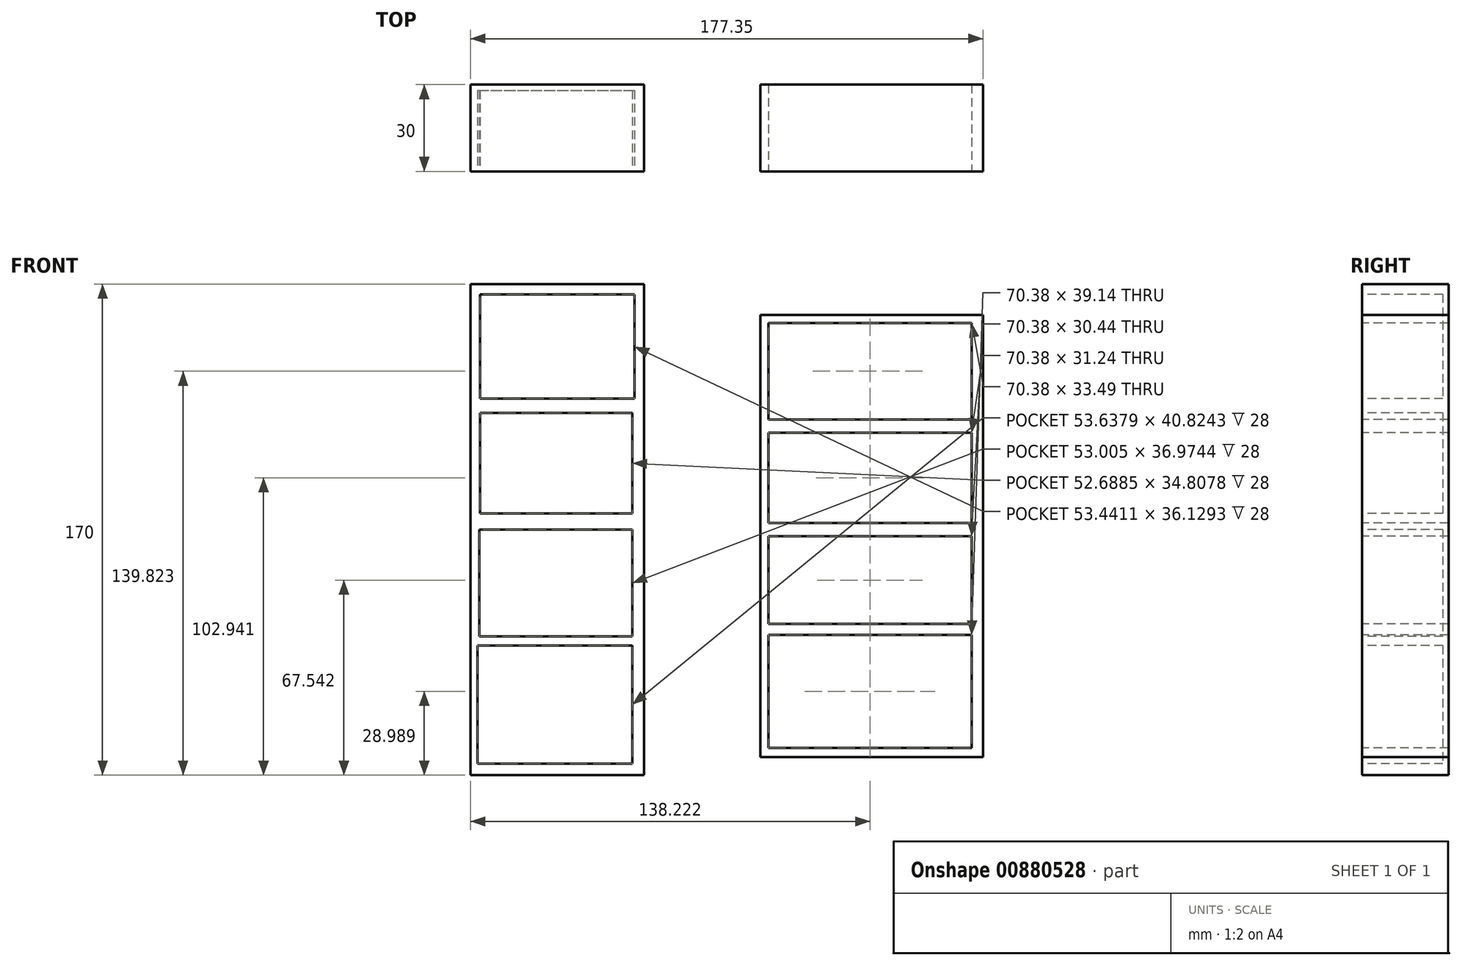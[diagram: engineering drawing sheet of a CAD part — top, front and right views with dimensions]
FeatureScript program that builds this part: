
annotation { "Feature Type Name" : "Feature", "Feature Type Description" : "" }
export const myFeature = defineFeature(function(context is Context, id is Id, definition is map)
    precondition{}
    {
        {
            var Q0;
            Q0=qCreatedBy(makeId("Front.planeOp"),FACE);
            var sketch = newSketch(context, id + "F0", { "sketchPlane" : qUnion([Q0])});
            skLineSegment(sketch, "E0.bottom", {"start": v(-219.84, 79.38) * mm, "end": v(-159.84, 79.38) * mm});
            skLineSegment(sketch, "E0.top", {"start": v(-219.84, -90.62) * mm, "end": v(-159.84, -90.62) * mm});
            skLineSegment(sketch, "E0.left", {"start": v(-219.84, 79.38) * mm, "end": v(-219.84, -90.62) * mm});
            skLineSegment(sketch, "E0.right", {"start": v(-159.84, 79.38) * mm, "end": v(-159.84, -90.62) * mm});
            skSolve(sketch);
        }
        {
            var Q0;
            Q0=makeQuery(id+"F0.imprint","IMPRINT",FACE,{"disambiguationData":[TD([[makeQuery(id+"F0.imprint","IMPRINT",EDGE,{"derivedFrom":sQuery(id+"F0.wireOp",EDGE,"E0.bottom")}),-1.0]])]});
            extrude(context, id + "F1", {"entities" : qUnion([Q0]), "depth" : 30 * mm, "offsetDistance" : 25 * mm});
        }
        {
            var Q0;
            Q0=makeQuery(id+"F1.opExtrude","CAP_FACE",FACE,{"disambiguationData":[OSD([sQuery(id+"F0.wireOp",EDGE,"E0.bottom"),sQuery(id+"F0.wireOp",EDGE,"E0.top"),sQuery(id+"F0.wireOp",EDGE,"E0.left"),sQuery(id+"F0.wireOp",EDGE,"E0.right")])],"isStart":false});
            var sketch = newSketch(context, id + "F2", { "sketchPlane" : qUnion([Q0])});
            skLineSegment(sketch, "E1.bottom", {"start": v(-216.5, 75.83) * mm, "end": v(-163.07, 75.83) * mm});
            skLineSegment(sketch, "E1.top", {"start": v(-216.5, 39.7) * mm, "end": v(-163.07, 39.7) * mm});
            skLineSegment(sketch, "E1.left", {"start": v(-216.5, 75.83) * mm, "end": v(-216.5, 39.7) * mm});
            skLineSegment(sketch, "E1.right", {"start": v(-163.07, 75.83) * mm, "end": v(-163.07, 39.7) * mm});
            skLineSegment(sketch, "E2.bottom", {"start": v(-216.5, 34.8) * mm, "end": v(-163.82, 34.8) * mm});
            skLineSegment(sketch, "E2.top", {"start": v(-216.5, 0) * mm, "end": v(-163.82, 0) * mm});
            skLineSegment(sketch, "E2.left", {"start": v(-216.5, 34.8) * mm, "end": v(-216.5, 0) * mm});
            skLineSegment(sketch, "E2.right", {"start": v(-163.82, 34.8) * mm, "end": v(-163.82, 0) * mm});
            skPoint(sketch, "E3.firstSnap0", {"position": v(-219.84, -5.62) * mm});
            skLineSegment(sketch, "E3.bottom", {"start": v(-216.83, -5.62) * mm, "end": v(-163.82, -5.62) * mm});
            skLineSegment(sketch, "E3.top", {"start": v(-216.83, -42.6) * mm, "end": v(-163.82, -42.6) * mm});
            skLineSegment(sketch, "E3.left", {"start": v(-216.83, -5.62) * mm, "end": v(-216.83, -42.6) * mm});
            skLineSegment(sketch, "E3.right", {"start": v(-163.82, -5.62) * mm, "end": v(-163.82, -42.6) * mm});
            skLineSegment(sketch, "E4.bottom", {"start": v(-217.46, -45.76) * mm, "end": v(-163.82, -45.76) * mm});
            skLineSegment(sketch, "E4.top", {"start": v(-217.46, -86.59) * mm, "end": v(-163.82, -86.59) * mm});
            skLineSegment(sketch, "E4.left", {"start": v(-217.46, -45.76) * mm, "end": v(-217.46, -86.59) * mm});
            skLineSegment(sketch, "E4.right", {"start": v(-163.82, -45.76) * mm, "end": v(-163.82, -86.59) * mm});
            skSolve(sketch);
        }
        {
            var Q0;
            Q0=makeQuery(id+"F2.imprint","IMPRINT",FACE,{"disambiguationData":[TD([[makeQuery(id+"F2.imprint","IMPRINT",EDGE,{"derivedFrom":sQuery(id+"F2.wireOp",EDGE,"E1.bottom")}),-1.0]])]});
            var Q1;
            Q1=makeQuery(id+"F2.imprint","IMPRINT",FACE,{"disambiguationData":[TD([[makeQuery(id+"F2.imprint","IMPRINT",EDGE,{"derivedFrom":sQuery(id+"F2.wireOp",EDGE,"E2.bottom")}),-1.0]])]});
            var Q2;
            Q2=makeQuery(id+"F2.imprint","IMPRINT",FACE,{"disambiguationData":[TD([[makeQuery(id+"F2.imprint","IMPRINT",EDGE,{"derivedFrom":sQuery(id+"F2.wireOp",EDGE,"E3.bottom")}),-1.0]])]});
            var Q3;
            Q3=makeQuery(id+"F2.imprint","IMPRINT",FACE,{"disambiguationData":[TD([[makeQuery(id+"F2.imprint","IMPRINT",EDGE,{"derivedFrom":sQuery(id+"F2.wireOp",EDGE,"E4.bottom")}),-1.0]])]});
            extrude(context, id + "F3", {"entities" : qUnion([Q0, Q1, Q2, Q3]), "operationType" : NewBodyOperationType.REMOVE, "oppositeDirection" : true, "depth" : 28 * mm, "offsetDistance" : 25 * mm});
        }
        {
            var Q0;
            Q0=qCreatedBy(makeId("Front.planeOp"),FACE);
            var sketch = newSketch(context, id + "F4", { "sketchPlane" : qUnion([Q0])});
            skLineSegment(sketch, "E5.bottom", {"start": v(-119.49, 68.64) * mm, "end": v(-42.49, 68.64) * mm});
            skLineSegment(sketch, "E5.top", {"start": v(-119.49, -84.36) * mm, "end": v(-42.49, -84.36) * mm});
            skLineSegment(sketch, "E5.left", {"start": v(-119.49, 68.64) * mm, "end": v(-119.49, -84.36) * mm});
            skLineSegment(sketch, "E5.right", {"start": v(-42.49, 68.64) * mm, "end": v(-42.49, -84.36) * mm});
            skSolve(sketch);
        }
        {
            var Q0;
            Q0=makeQuery(id+"F4.imprint","IMPRINT",FACE,{"disambiguationData":[TD([[makeQuery(id+"F4.imprint","IMPRINT",EDGE,{"derivedFrom":sQuery(id+"F4.wireOp",EDGE,"E5.bottom")}),-1.0]])]});
            extrude(context, id + "F5", {"entities" : qUnion([Q0]), "depth" : 30 * mm, "offsetDistance" : 25 * mm});
        }
        {
            var Q0;
            Q0=makeQuery(id+"F5.opExtrude","CAP_FACE",FACE,{"disambiguationData":[OSD([sQuery(id+"F4.wireOp",EDGE,"E5.bottom"),sQuery(id+"F4.wireOp",EDGE,"E5.top"),sQuery(id+"F4.wireOp",EDGE,"E5.left"),sQuery(id+"F4.wireOp",EDGE,"E5.right")])],"isStart":false});
            var sketch = newSketch(context, id + "F6", { "sketchPlane" : qUnion([Q0])});
            skLineSegment(sketch, "E6.bottom", {"start": v(-116.8, 65.95) * mm, "end": v(-46.43, 65.95) * mm});
            skLineSegment(sketch, "E6.top", {"start": v(-116.8, 32.46) * mm, "end": v(-46.43, 32.46) * mm});
            skLineSegment(sketch, "E6.left", {"start": v(-116.8, 65.95) * mm, "end": v(-116.8, 32.46) * mm});
            skLineSegment(sketch, "E6.right", {"start": v(-46.43, 65.95) * mm, "end": v(-46.43, 32.46) * mm});
            skLineSegment(sketch, "E7.bottom", {"start": v(-116.8, 27.94) * mm, "end": v(-46.43, 27.94) * mm});
            skLineSegment(sketch, "E7.top", {"start": v(-116.8, -3.3) * mm, "end": v(-46.43, -3.3) * mm});
            skLineSegment(sketch, "E7.left", {"start": v(-116.8, 27.94) * mm, "end": v(-116.8, -3.3) * mm});
            skLineSegment(sketch, "E7.right", {"start": v(-46.43, 27.94) * mm, "end": v(-46.43, -3.3) * mm});
            skPoint(sketch, "E8.firstSnap0", {"position": v(-119.49, -7.86) * mm});
            skLineSegment(sketch, "E8.bottom", {"start": v(-116.8, -7.86) * mm, "end": v(-46.43, -7.86) * mm});
            skLineSegment(sketch, "E8.top", {"start": v(-116.8, -38.3) * mm, "end": v(-46.43, -38.3) * mm});
            skLineSegment(sketch, "E8.left", {"start": v(-116.8, -7.86) * mm, "end": v(-116.8, -38.3) * mm});
            skLineSegment(sketch, "E8.right", {"start": v(-46.43, -7.86) * mm, "end": v(-46.43, -38.3) * mm});
            skLineSegment(sketch, "E9.bottom", {"start": v(-116.8, -42.06) * mm, "end": v(-46.43, -42.06) * mm});
            skLineSegment(sketch, "E9.top", {"start": v(-116.8, -81.2) * mm, "end": v(-46.43, -81.2) * mm});
            skLineSegment(sketch, "E9.left", {"start": v(-116.8, -42.06) * mm, "end": v(-116.8, -81.2) * mm});
            skLineSegment(sketch, "E9.right", {"start": v(-46.43, -42.06) * mm, "end": v(-46.43, -81.2) * mm});
            skSolve(sketch);
        }
        {
            var Q0;
            Q0=makeQuery(id+"F6.imprint","IMPRINT",FACE,{"disambiguationData":[TD([[makeQuery(id+"F6.imprint","IMPRINT",EDGE,{"derivedFrom":sQuery(id+"F6.wireOp",EDGE,"E6.bottom")}),-1.0]])]});
            var Q1;
            Q1=makeQuery(id+"F6.imprint","IMPRINT",FACE,{"disambiguationData":[TD([[makeQuery(id+"F6.imprint","IMPRINT",EDGE,{"derivedFrom":sQuery(id+"F6.wireOp",EDGE,"E7.bottom")}),-1.0]])]});
            var Q2;
            Q2=makeQuery(id+"F6.imprint","IMPRINT",FACE,{"disambiguationData":[TD([[makeQuery(id+"F6.imprint","IMPRINT",EDGE,{"derivedFrom":sQuery(id+"F6.wireOp",EDGE,"E8.bottom")}),-1.0]])]});
            var Q3;
            Q3=makeQuery(id+"F6.imprint","IMPRINT",FACE,{"disambiguationData":[TD([[makeQuery(id+"F6.imprint","IMPRINT",EDGE,{"derivedFrom":sQuery(id+"F6.wireOp",EDGE,"E9.bottom")}),-1.0]])]});
            extrude(context, id + "F7", {"entities" : qUnion([Q0, Q1, Q2, Q3]), "operationType" : NewBodyOperationType.REMOVE, "oppositeDirection" : true, "depth" : 30 * mm, "offsetDistance" : 25 * mm});
        }
    });
